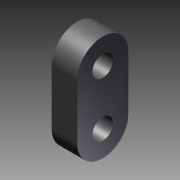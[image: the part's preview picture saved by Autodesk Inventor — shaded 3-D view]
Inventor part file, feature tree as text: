
AUTODESK INVENTOR PART (.ipt)
format: ipt  version: 2011 SP1 (Build 150282100, 282)  size: 91,648 bytes
history: native  units: mm
features: other x14, sketch x3, revolve x2, extrude x1
ambient origin geometry x8: Origin, YZ Plane, XZ Plane, XY Plane, X Axis, Y Axis, Z Axis, Center Point
bodies: Solid1 (feature_tree)
feature tree (20):
  extrude  "Extrusion1"  TaperAngle=360.0deg  [1 undecoded]
  revolve  "Revolution1"  [1 undecoded]
  revolve  "Revolution2"  [1 undecoded]
  other  "ZS1_XY"
  other  "ZS1_YZ"
  other  "ZS1_ZX"
  other  "ZS1_X"
  other  "ZS1_Y"
  other  "ZS1_Z"
  other  "ZS1_Center"
  other  "ZS2_XY"
  other  "ZS2_YZ"
  other  "ZS2_ZX"
  other  "ZS2_X"
  other  "ZS2_Y"
  other  "ZS2_Z"
  other  "ZS2_Center"
  sketch  "Skizze_1"  dims[d0=3.0mm d1=0.0mm d2=360.0deg]
  sketch  "Skizze_2"  dims[d3=360.0deg]
  sketch  "Skizze_3"
note: 3 required parameter values undecoded (feature->parameter linkage not recoverable at this tier; creation-order binding heuristic only, values carry confidence <= 0.55)
